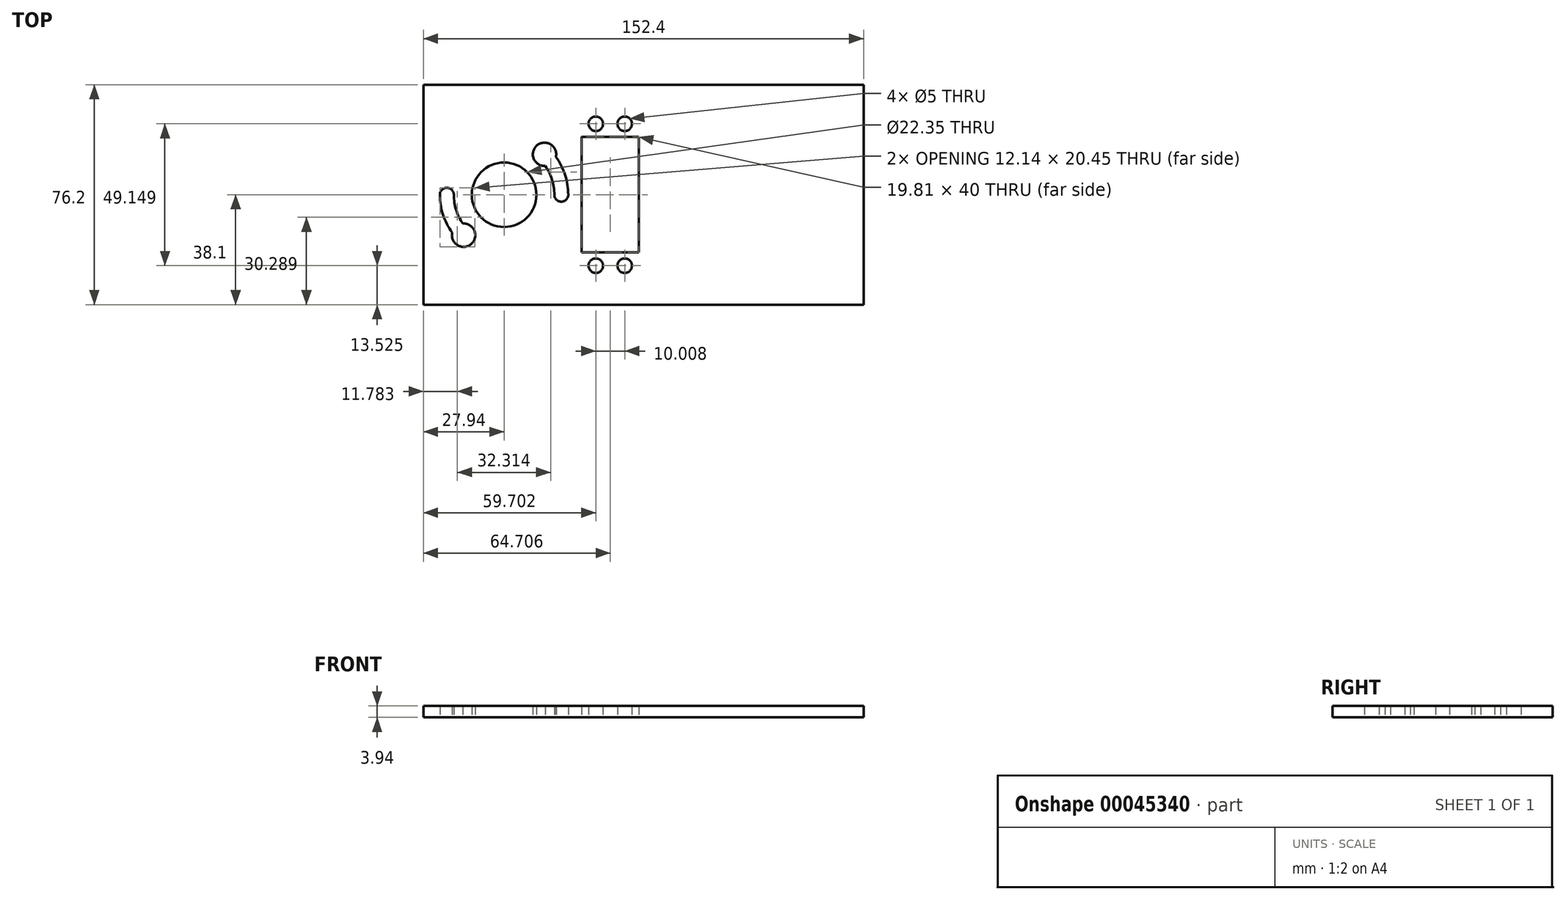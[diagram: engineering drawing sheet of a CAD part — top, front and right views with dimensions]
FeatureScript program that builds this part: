
annotation { "Feature Type Name" : "Feature", "Feature Type Description" : "" }
export const myFeature = defineFeature(function(context is Context, id is Id, definition is map)
    precondition{}
    {
        {
            var Q0;
            Q0=qCreatedBy(makeId("Top.planeOp"),FACE);
            var sketch = newSketch(context, id + "F0", { "sketchPlane" : qUnion([Q0])});
            skLineSegment(sketch, "E0.bottom", {"start": v(0, 0) * mm, "end": v(152.4, 0) * mm});
            skLineSegment(sketch, "E0.top", {"start": v(0, 76.2) * mm, "end": v(152.4, 76.2) * mm});
            skLineSegment(sketch, "E0.left", {"start": v(0, 0) * mm, "end": v(0, 76.2) * mm});
            skLineSegment(sketch, "E0.right", {"start": v(152.4, 0) * mm, "end": v(152.4, 76.2) * mm});
            skCircle(sketch, "E1", {"center": v(27.94, 38.1) * mm, "radius": 11.18 * mm});
            skLineSegment(sketch, "E2", {"start": v(27.94, 76.2) * mm, "end": v(27.94, 0) * mm, "construction": true});
            skLineSegment(sketch, "E3", {"start": v(0, 38.1) * mm, "end": v(152.4, 38.1) * mm, "construction": true});
            skLineSegment(sketch, "E4", {"start": v(27.94, 38.1) * mm, "end": v(41.95, 52.1) * mm, "construction": true});
            skLineSegment(sketch, "E5", {"start": v(27.94, 38.1) * mm, "end": v(47.75, 38.1) * mm, "construction": true});
            skLineSegment(sketch, "E6", {"start": v(13.93, 24.1) * mm, "end": v(27.94, 38.1) * mm, "construction": true});
            skLineSegment(sketch, "E7", {"start": v(27.94, 38.1) * mm, "end": v(8.13, 38.1) * mm, "construction": true});
            skCircle(sketch, "E8", {"center": v(47.75, 38.1) * mm, "radius": 2.41 * mm});
            skCircle(sketch, "E9", {"center": v(8.13, 38.1) * mm, "radius": 2.41 * mm});
            skCircle(sketch, "E10", {"center": v(41.95, 52.1) * mm, "radius": 2.41 * mm});
            skCircle(sketch, "E11", {"center": v(13.93, 24.1) * mm, "radius": 2.41 * mm});
            skArc(sketch, "E12", {"start": v(15.64, 25.8) * mm, "mid": v(11.87, 31.44) * mm, "end": v(10.54, 38.1) * mm});
            skArc(sketch, "E13", {"start": v(12.22, 22.38) * mm, "mid": v(7.4, 29.6) * mm, "end": v(5.72, 38.1) * mm});
            skArc(sketch, "E14", {"start": v(40.24, 50.4) * mm, "mid": v(44.01, 44.76) * mm, "end": v(45.34, 38.1) * mm});
            skArc(sketch, "E15", {"start": v(43.66, 53.82) * mm, "mid": v(48.47, 46.6) * mm, "end": v(50.17, 38.1) * mm});
            skCircle(sketch, "E16", {"center": v(41.95, 52.1) * mm, "radius": 4.04 * mm});
            skCircle(sketch, "E17", {"center": v(13.93, 24.1) * mm, "radius": 4.04 * mm});
            skLineSegment(sketch, "E18.bottom", {"start": v(54.8, 18.1) * mm, "end": v(74.61, 18.1) * mm});
            skLineSegment(sketch, "E18.top", {"start": v(54.8, 58.1) * mm, "end": v(74.61, 58.1) * mm});
            skLineSegment(sketch, "E18.left", {"start": v(54.8, 18.1) * mm, "end": v(54.8, 58.1) * mm});
            skLineSegment(sketch, "E18.right", {"start": v(74.61, 18.1) * mm, "end": v(74.61, 58.1) * mm});
            skLineSegment(sketch, "E19", {"start": v(54.8, 38.1) * mm, "end": v(74.61, 38.1) * mm, "construction": true});
            skLineSegment(sketch, "E20", {"start": v(64.7, 13.53) * mm, "end": v(64.7, 62.67) * mm, "construction": true});
            skPoint(sketch, "E20.startSnap0", {"position": v(64.7, 18.1) * mm});
            skLineSegment(sketch, "E21", {"start": v(54.8, 28.1) * mm, "end": v(74.61, 28.1) * mm, "construction": true});
            skCircle(sketch, "E22", {"center": v(64.7, 28.1) * mm, "radius": 2.86 * mm});
            skLineSegment(sketch, "E23", {"start": v(54.8, 62.67) * mm, "end": v(74.61, 62.67) * mm, "construction": true});
            skLineSegment(sketch, "E24", {"start": v(54.8, 13.53) * mm, "end": v(74.61, 13.53) * mm, "construction": true});
            skLineSegment(sketch, "E25", {"start": v(69.7, 62.67) * mm, "end": v(69.7, 13.53) * mm, "construction": true});
            skLineSegment(sketch, "E26", {"start": v(59.7, 62.67) * mm, "end": v(59.7, 13.53) * mm, "construction": true});
            skCircle(sketch, "E27", {"center": v(69.7, 62.67) * mm, "radius": 2.5 * mm});
            skCircle(sketch, "E28", {"center": v(59.7, 62.67) * mm, "radius": 2.5 * mm});
            skCircle(sketch, "E29", {"center": v(69.7, 13.53) * mm, "radius": 2.5 * mm});
            skCircle(sketch, "E30", {"center": v(59.7, 13.53) * mm, "radius": 2.5 * mm});
            skSolve(sketch);
        }
        {
            var Q0;
            Q0=makeQuery(id+"F0.imprint","IMPRINT",FACE,{"disambiguationData":[TD([[makeQuery(id+"F0.imprint","IMPRINT",EDGE,{"derivedFrom":sQuery(id+"F0.wireOp",EDGE,"E0.bottom")}),1.0]])]});
            extrude(context, id + "F1", {"entities" : qUnion([Q0]), "depth" : 3.94 * mm});
        }
    });
